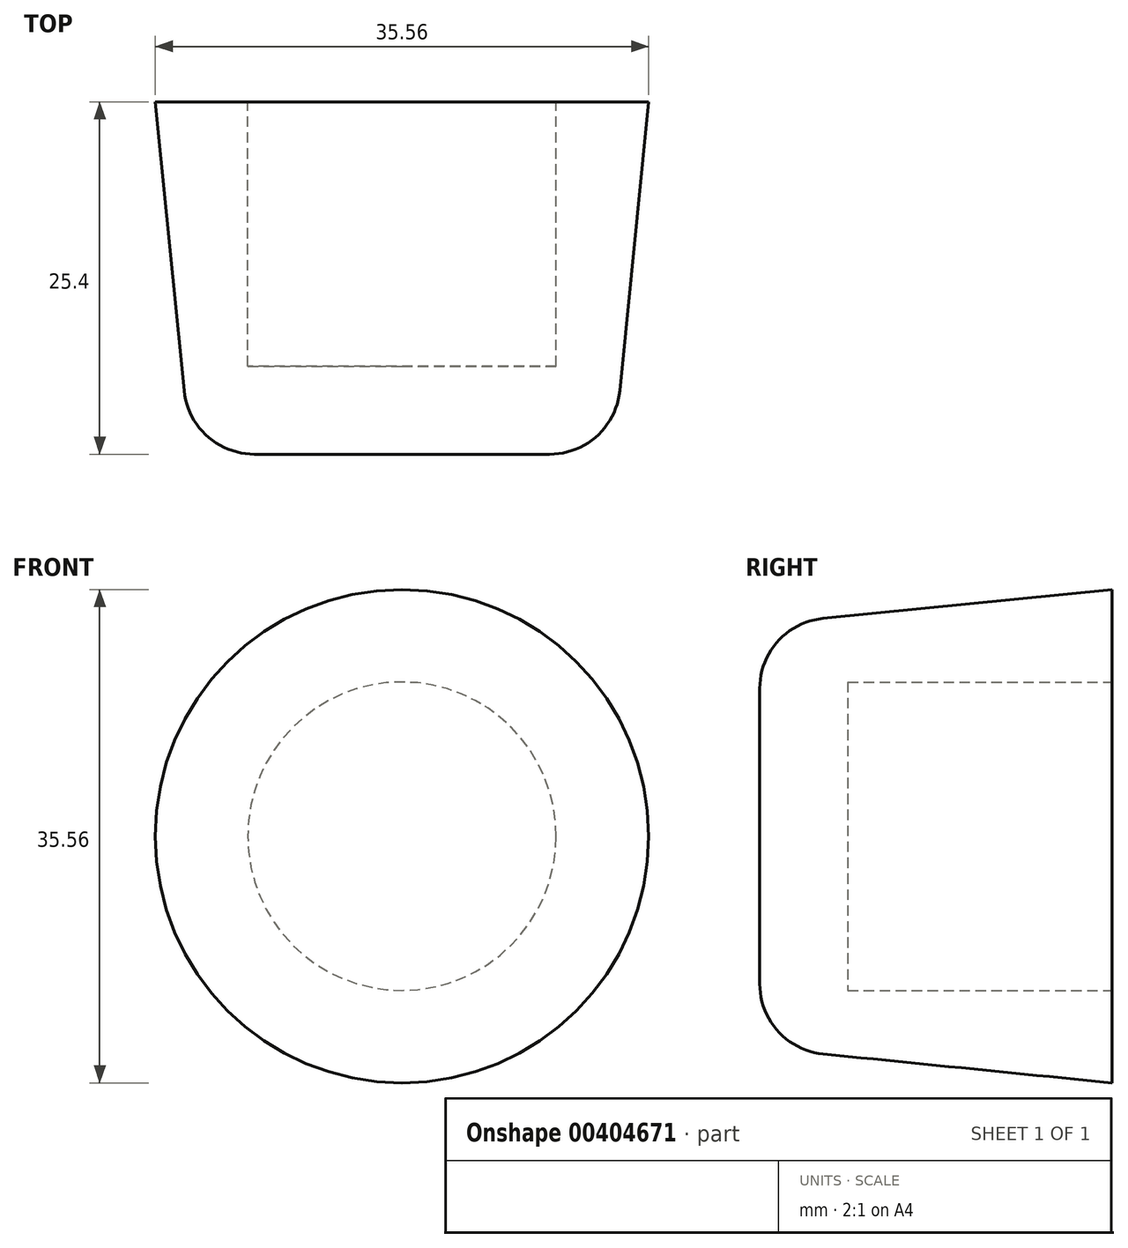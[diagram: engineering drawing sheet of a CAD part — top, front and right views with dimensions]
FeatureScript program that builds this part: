
annotation { "Feature Type Name" : "Feature", "Feature Type Description" : "" }
export const myFeature = defineFeature(function(context is Context, id is Id, definition is map)
    precondition{}
    {
        {
            var Q0;
            Q0=qCreatedBy(makeId("Front.planeOp"),FACE);
            var sketch = newSketch(context, id + "F0", { "sketchPlane" : qUnion([Q0])});
            skCircle(sketch, "E0", {"center": v(0, 0) * mm, "radius": 17.78 * mm});
            skSolve(sketch);
        }
        {
            var Q0;
            Q0=qCreatedBy(makeId("Front.planeOp"),FACE);
            cPlane(context, id + "F1", {"entities" : qUnion([Q0]), "cplaneType" : CPlaneType.OFFSET, "offset" : 25.4 * mm, "width" : 152.4 * mm, "height" : 152.4 * mm});
        }
        {
            var Q0;
            Q0=qCreatedBy(id+"F1.planeOp",FACE);
            var sketch = newSketch(context, id + "F2", { "sketchPlane" : qUnion([Q0])});
            skCircle(sketch, "E1", {"center": v(0, 0) * mm, "radius": 15.24 * mm});
            skSolve(sketch);
        }
        {
            var Q0;
            Q0=makeQuery(id+"F0.imprint","IMPRINT",FACE,{"disambiguationData":[TD([[makeQuery(id+"F0.imprint","IMPRINT",EDGE,{"derivedFrom":sQuery(id+"F0.wireOp",EDGE,"E0")}),1.0]])]});
            var Q1;
            Q1=makeQuery(id+"F2.imprint","IMPRINT",FACE,{"disambiguationData":[TD([[makeQuery(id+"F2.imprint","IMPRINT",EDGE,{"derivedFrom":sQuery(id+"F2.wireOp",EDGE,"E1")}),1.0]])]});
            loft(context, id + "F3", {"sheetProfilesArray" : [{ "sheetProfileEntities" : qUnion([Q0]) }, { "sheetProfileEntities" : qUnion([Q1]) }]});
        }
        {
            var Q0;
            Q0=makeQuery(id+"F3.opLoft","MID_CAP_EDGE",EDGE,{"disambiguationData":[OSD([sQuery(id+"F0.wireOp",EDGE,"E0"),sQuery(id+"F2.wireOp",EDGE,"E1")])],"capPos":1.0});
            fillet(context, id + "F4", {"entities" : qUnion([Q0]), "radius" : 5.08 * mm, "tangentPropagation" : true, "allowEdgeOverflow" : false});
        }
        {
            var Q0;
            Q0=makeQuery(id+"F3.opLoft","CAP_FACE",FACE,{"disambiguationData":[OSD([makeQuery(id+"F0.imprint","IMPRINT",FACE,{"disambiguationData":[TD([[makeQuery(id+"F0.imprint","IMPRINT",EDGE,{"derivedFrom":sQuery(id+"F0.wireOp",EDGE,"E0")}),1.0]])]})])],"isStart":true});
            var sketch = newSketch(context, id + "F5", { "sketchPlane" : qUnion([Q0])});
            skCircle(sketch, "E2", {"center": v(0, 0) * mm, "radius": 11.11 * mm});
            skSolve(sketch);
        }
        {
            var Q0;
            Q0=makeQuery(id+"F5.imprint","IMPRINT",FACE,{"disambiguationData":[TD([[makeQuery(id+"F5.imprint","IMPRINT",EDGE,{"derivedFrom":sQuery(id+"F5.wireOp",EDGE,"E2")}),1.0]])]});
            extrude(context, id + "F6", {"entities" : qUnion([Q0]), "operationType" : NewBodyOperationType.REMOVE, "oppositeDirection" : true, "depth" : 19.05 * mm});
        }
    });
